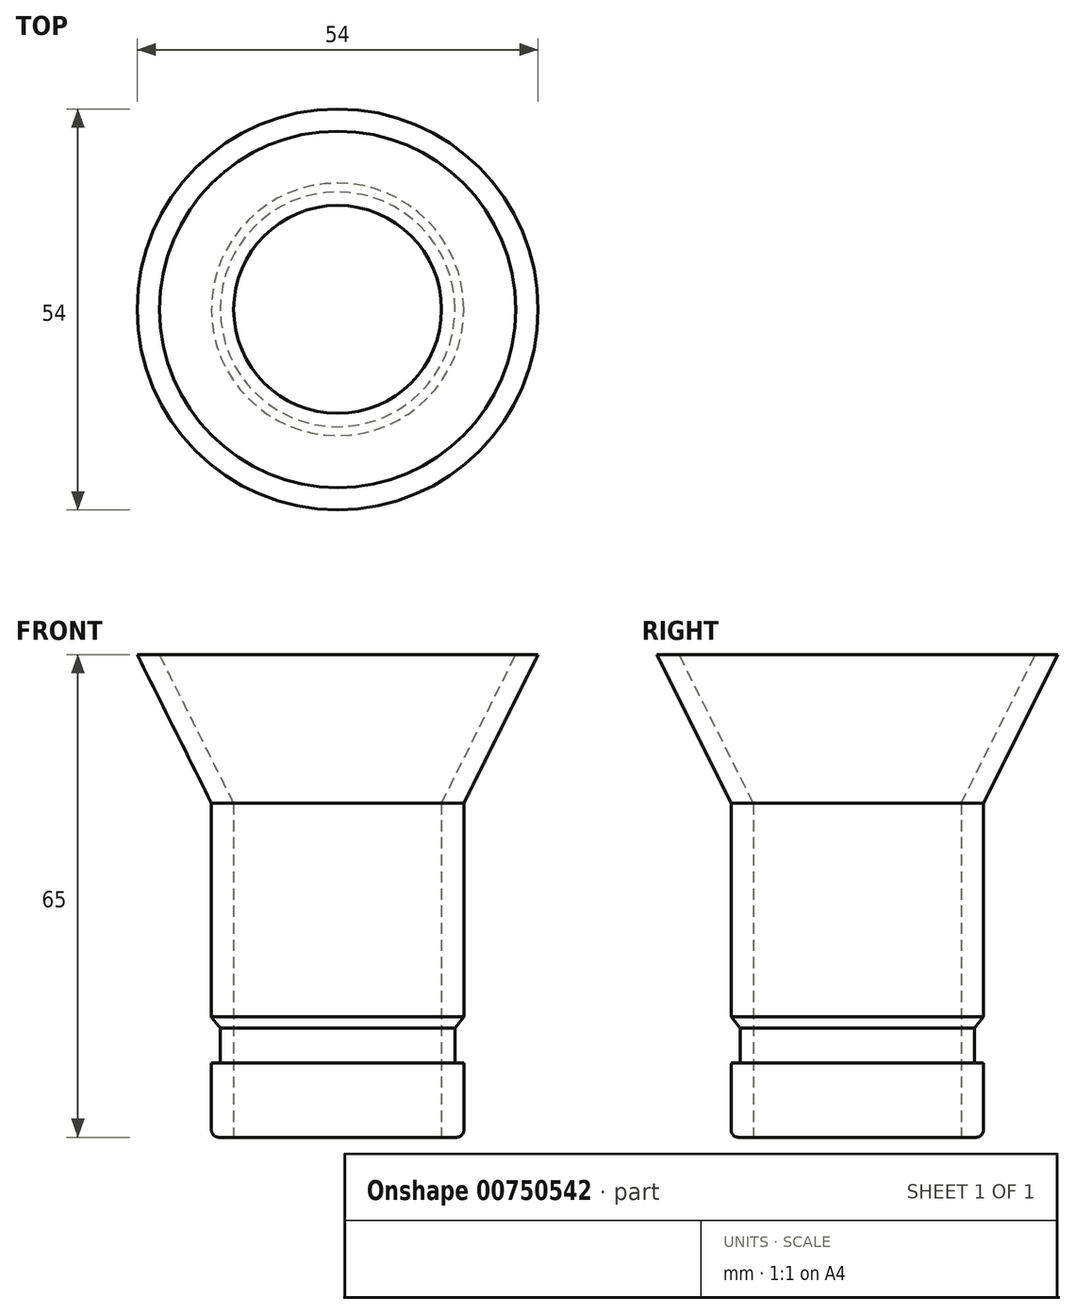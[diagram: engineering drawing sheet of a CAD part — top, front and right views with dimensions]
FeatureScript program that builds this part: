
annotation { "Feature Type Name" : "Feature", "Feature Type Description" : "" }
export const myFeature = defineFeature(function(context is Context, id is Id, definition is map)
    precondition{}
    {
        {
            var Q0;
            Q0=qCreatedBy(makeId("Right.planeOp"),FACE);
            var sketch = newSketch(context, id + "F0", { "sketchPlane" : qUnion([Q0])});
            skLineSegment(sketch, "E0", {"start": v(14, 0) * mm, "end": v(17, 0) * mm});
            skLineSegment(sketch, "E1", {"start": v(17, 0) * mm, "end": v(17, 10) * mm});
            skLineSegment(sketch, "E2", {"start": v(0, 0) * mm, "end": v(0, 45) * mm});
            skLineSegment(sketch, "E3", {"start": v(17, 45) * mm, "end": v(17, 16.2) * mm});
            skLineSegment(sketch, "E4", {"start": v(17, 16.2) * mm, "end": v(15.8, 14.7) * mm});
            skLineSegment(sketch, "E5", {"start": v(15.8, 14.7) * mm, "end": v(15.8, 10) * mm});
            skLineSegment(sketch, "E6", {"start": v(15.8, 10) * mm, "end": v(17, 10) * mm});
            skLineSegment(sketch, "E7", {"start": v(14, 45) * mm, "end": v(14, 0) * mm});
            skLineSegment(sketch, "E8", {"start": v(24, 65) * mm, "end": v(27, 65) * mm});
            skLineSegment(sketch, "E9", {"start": v(27, 65) * mm, "end": v(17, 45) * mm});
            skLineSegment(sketch, "E10", {"start": v(24, 65) * mm, "end": v(14, 45) * mm});
            skSolve(sketch);
        }
        {
            var Q0;
            Q0=makeQuery(id+"F0.imprint","IMPRINT",FACE,{"disambiguationData":[TD([[makeQuery(id+"F0.imprint","IMPRINT",EDGE,{"derivedFrom":sQuery(id+"F0.wireOp",EDGE,"E0")}),1.0]])]});
            var Q1;
            Q1=sQuery(id+"F0.wireOp",EDGE,"E2");
            revolve(context, id + "F1", {"surfaceOperationType" : NewSurfaceOperationType.NEW, "entities" : qUnion([Q0]), "axis" : qUnion([Q1]), "revolveType" : RevolveType.FULL});
        }
        {
            var Q0;
            Q0=makeQuery(id+"F1.opRevolve","SWEPT_EDGE",EDGE,{"disambiguationData":[OSD([sQuery(id+"F0.wireOp",EDGE,"E0"),sQuery(id+"F0.wireOp",EDGE,"E1")])]});
            fillet(context, id + "F2", {"entities" : qUnion([Q0]), "radius" : 1 * mm, "tangentPropagation" : true, "allowEdgeOverflow" : false});
        }
    });
